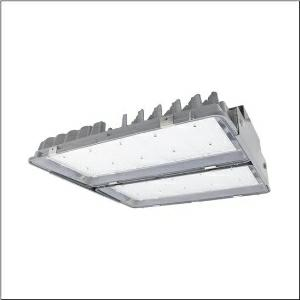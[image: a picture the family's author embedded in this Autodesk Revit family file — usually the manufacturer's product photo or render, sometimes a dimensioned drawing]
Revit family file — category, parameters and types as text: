
# Revit family: highbay_11xtreme_51hf62db4qma
name_source: partatom
category: Lighting Fixtures
units: mm (PartAtom-declared; Revit-internal decimal feet)

## family parameters
Cut with Voids When Loaded = No
Host = Face
Light Source = No
Part Type = Normal
Room Calculation Point = No
Round Connector Dimension = Use Diameter
Shared = No

## types (1)
- --- (1 x LED, 36800 lm, 193.7 W, 4000K)
    Apparent Load = 194 VA
    CIE Flux Codes = 84 96 100 100 100
    Color Rendering = 80
    Color Temperature = 4000K
    Default Elevation = 1800 mm
    Description = Highbay 11Xtreme, high bay luminaire, primary light control with lens, of PMMA, primary optical cover: cover, of toughened safety glass, light emission: direct distribution, primary light characteristic: symmetric, installation type: suspended mounting, surface-mounted, 2x LED module,for 1x 2x LED, rated luminous flux: 36.000lm, luminous efficacy: 178lm/W, light colour: 840, colour temperature: 4000K, control gear: DALI 2 (with two DALI addresses), with cable H07RN-F 5x 1.5mm², mains connection: 220..240V, AC, 50/60Hz, cable length: 1,5m, rated input power: 202W, luminaire housing, of diecast aluminium, coated, silver, length: 595mm, width: 560mm, height: 195mm, protection rating (complete): IP66, insulation class (complete): insulation class I (protective earthing), certification: CE, ENEC, UKCA, protection symbol: D, ball protection: ball impact resistant according to DIN VDE 0710 part 13 (with chain suspension), impact resistance: IK08, permissible operating ambient temperature: -25..+70°C, reducing of maximum allowable ambient temperature of 5°C with ceiling mounting, packaging unit: 1 piece
    Height = 157 mm
    Lamp = 1 x LED
    Lamp Light Flux = 36800 lm
    Lamp Power = 193.7 W
    Lamp count = 1
    Length = 593 mm
    Luminous efficacy = 190 lm/W
    Manufacturer = Siteco
    ModVariant = No
    Model = 51HF62DB4QMA
    Mounting Place = Ceiling
    Mounting Type = Pendant
    Number of Poles = 1
    OnlyDefault = Yes
    Power Factor = 1
    Product Name = Highbay 11Xtreme
    Product group = high bay luminaire
    ProductGroupID = 902
    Protection Class = Protection class I
    Protection Degree = IP 66
    RLX_Detail_Level = 1
    RLX_Emergency_Light_Flux = 0 lm
    RLX_Emergency_Type = 0
    RLX_Emergency_Type_DB = No
    RlxData = <blob elided: 34317 chars, md5=8722c918>
    Socket = socket
    Standby Power = 0 W
    System Light Flux = 36799 lm
    System Power = 194 W
    Type Comments = factory setting: luminous flux: 100 % | dim-lin: 254 | 648 mA
    Type Image = l_1258340.jpg
    URL = http://relux.com
    VarID = @adj_088323
    Voltage = 0 V
    Weight = 0.00 kg
    Width = 568 mm

## geometry (parser evidence)
native form markers: Blend x4, Sweep x11
no freeform markers — native parametric forms only
